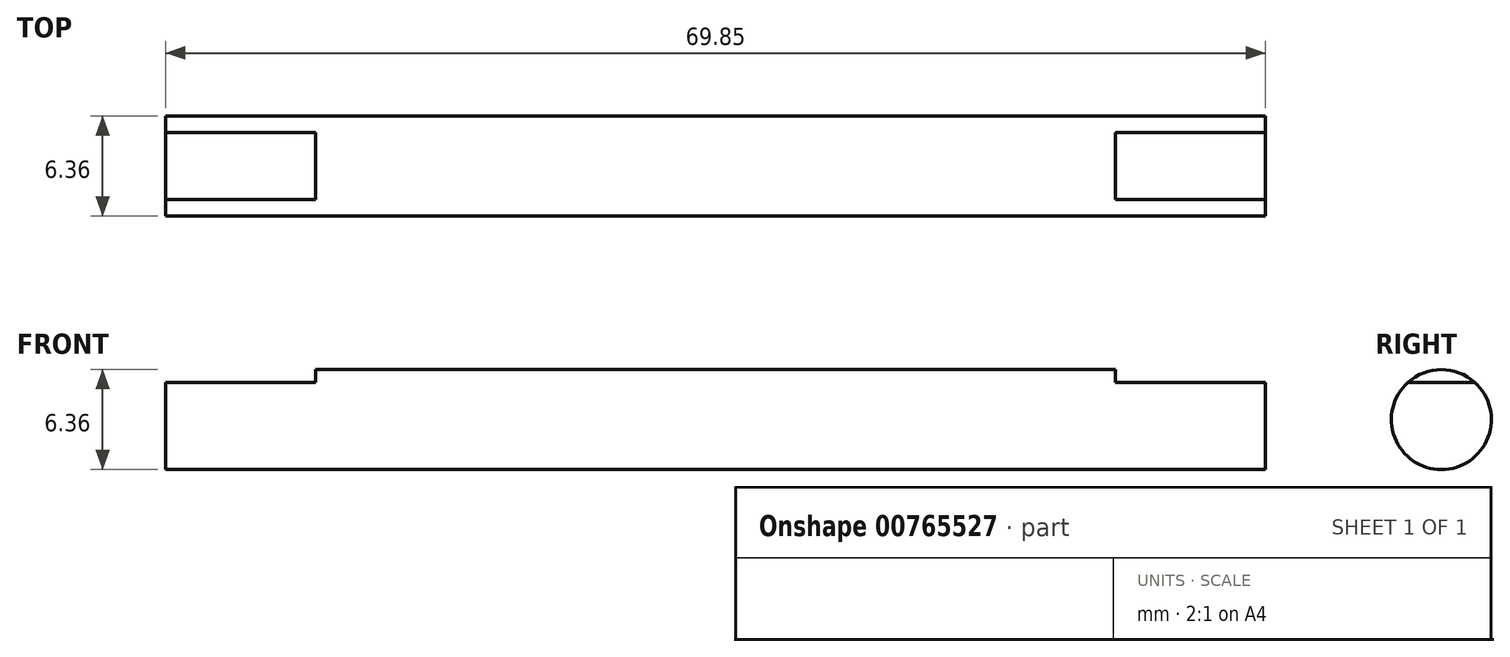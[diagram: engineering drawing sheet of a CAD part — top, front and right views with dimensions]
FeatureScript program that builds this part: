
annotation { "Feature Type Name" : "Feature", "Feature Type Description" : "" }
export const myFeature = defineFeature(function(context is Context, id is Id, definition is map)
    precondition{}
    {
        {
            var Q0;
            Q0=qCreatedBy(makeId("Right.planeOp"),FACE);
            var sketch = newSketch(context, id + "F0", { "sketchPlane" : qUnion([Q0])});
            skCircle(sketch, "E0", {"center": v(0, 0) * mm, "radius": 3.18 * mm});
            skSolve(sketch);
        }
        {
            var Q0;
            Q0 = qSketchRegion(id + "F0", true);
            extrude(context, id + "F1", {"entities" : qUnion([Q0]), "depth" : 69.85 * mm, "offsetDistance" : 25.4 * mm});
        }
        {
            var Q0;
            Q0=qCreatedBy(makeId("Front.planeOp"),FACE);
            var sketch = newSketch(context, id + "F2", { "sketchPlane" : qUnion([Q0])});
            skLineSegment(sketch, "E1", {"start": v(0, 3.18) * mm, "end": v(69.85, 3.18) * mm});
            skLineSegment(sketch, "E2.bottom", {"start": v(0, 3.18) * mm, "end": v(9.53, 3.18) * mm});
            skLineSegment(sketch, "E2.top", {"start": v(0, 2.36) * mm, "end": v(9.53, 2.36) * mm});
            skLineSegment(sketch, "E2.left", {"start": v(0, 3.18) * mm, "end": v(0, 2.36) * mm});
            skLineSegment(sketch, "E2.right", {"start": v(9.53, 3.18) * mm, "end": v(9.53, 2.36) * mm});
            skLineSegment(sketch, "E3.0", {"start": v(69.85, 3.18) * mm, "end": v(69.85, -3.18) * mm});
            skLineSegment(sketch, "E4.bottom", {"start": v(69.85, 2.36) * mm, "end": v(60.33, 2.36) * mm});
            skLineSegment(sketch, "E4.top", {"start": v(69.85, 3.18) * mm, "end": v(60.33, 3.18) * mm});
            skLineSegment(sketch, "E4.left", {"start": v(69.85, 2.36) * mm, "end": v(69.85, 3.18) * mm});
            skLineSegment(sketch, "E4.right", {"start": v(60.33, 2.36) * mm, "end": v(60.33, 3.18) * mm});
            skSolve(sketch);
        }
        {
            var Q0;
            Q0 = qSketchRegion(id + "F2", true);
            extrude(context, id + "F3", {"entities" : qUnion([Q0]), "operationType" : NewBodyOperationType.REMOVE, "depth" : 25.4 * mm, "offsetDistance" : 25.4 * mm, "symmetric" : true});
        }
    });
